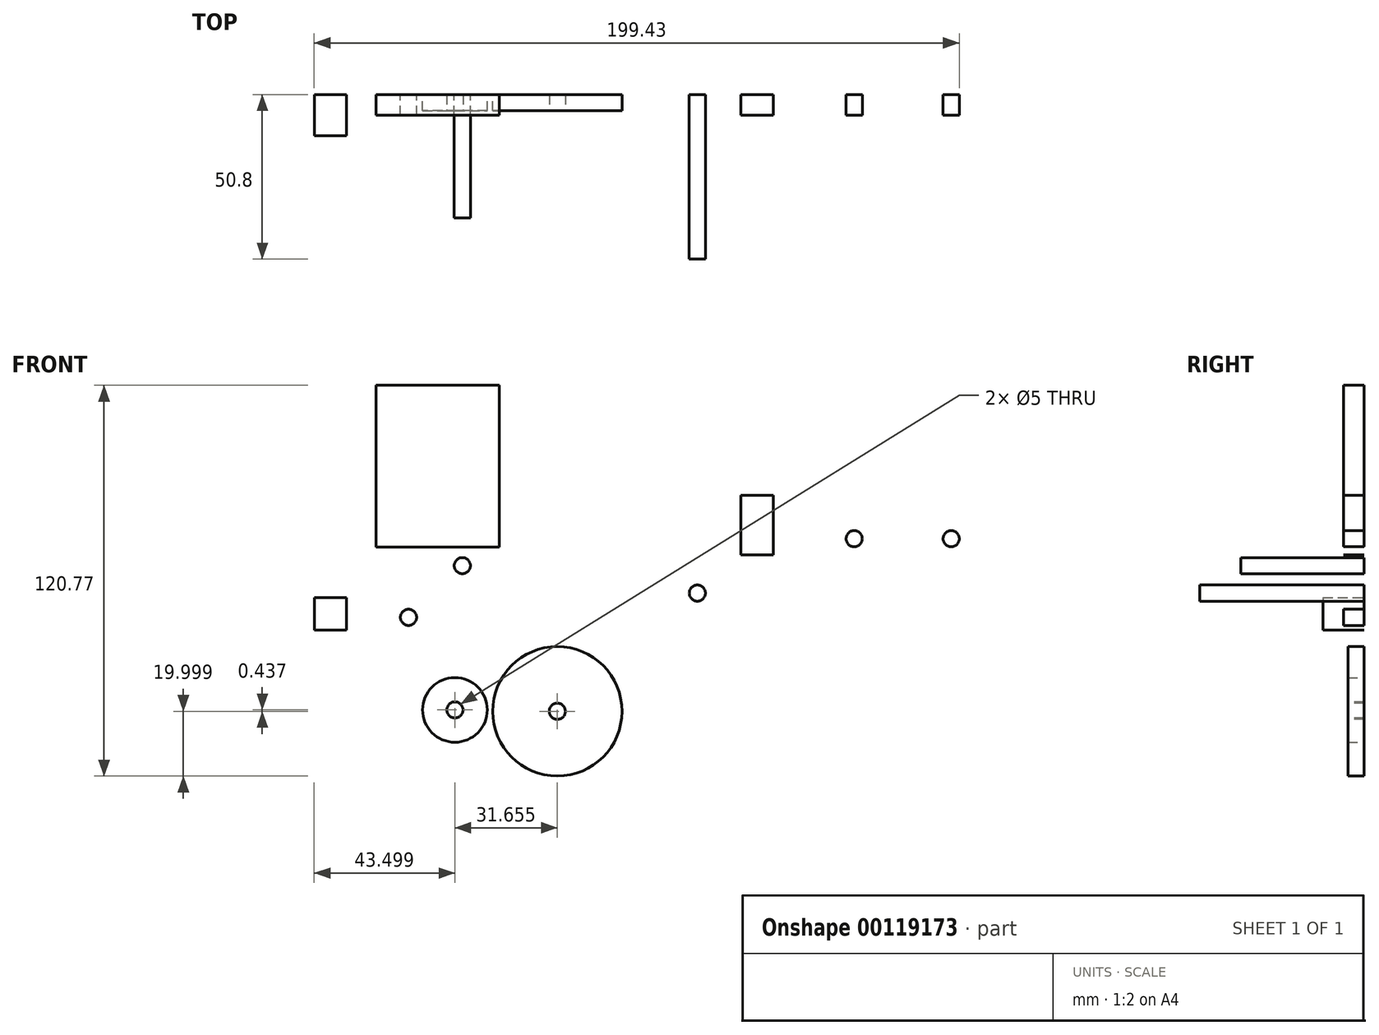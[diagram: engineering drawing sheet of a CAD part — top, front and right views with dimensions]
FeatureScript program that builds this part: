
annotation { "Feature Type Name" : "Feature", "Feature Type Description" : "" }
export const myFeature = defineFeature(function(context is Context, id is Id, definition is map)
    precondition{}
    {
        {
            var Q0;
            Q0=qCreatedBy(makeId("Front.planeOp"),FACE);
            var sketch = newSketch(context, id + "F0", { "sketchPlane" : qUnion([Q0])});
            skCircle(sketch, "E0", {"center": v(-47.6, -11.02) * mm, "radius": 10 * mm});
            skCircle(sketch, "E1", {"center": v(-15.94, -11.46) * mm, "radius": 20 * mm});
            skSolve(sketch);
        }
        {
            var Q0;
            Q0 = qSketchRegion(id + "F0", true);
            extrude(context, id + "F1", {"entities" : qUnion([Q0]), "depth" : 5 * mm});
        }
        {
            var Q0;
            Q0=makeQuery(id+"F1.opExtrude","CAP_FACE",FACE,{"disambiguationData":[OSD([sQuery(id+"F0.wireOp",EDGE,"E0")])],"isStart":false});
            var sketch = newSketch(context, id + "F2", { "sketchPlane" : qUnion([Q0])});
            skCircle(sketch, "E2", {"center": v(-47.6, -11.02) * mm, "radius": 2.5 * mm});
            skSolve(sketch);
        }
        {
            var Q0;
            Q0 = qSketchRegion(id + "F2", true);
            extrude(context, id + "F3", {"entities" : qUnion([Q0]), "operationType" : NewBodyOperationType.REMOVE, "endBound" : BoundingType.THROUGH_ALL, "oppositeDirection" : true, "depth" : 25.4 * mm});
        }
        {
            var Q0;
            Q0=makeQuery(id+"F1.opExtrude","CAP_FACE",FACE,{"disambiguationData":[OSD([sQuery(id+"F0.wireOp",EDGE,"E1")])],"isStart":false});
            var sketch = newSketch(context, id + "F4", { "sketchPlane" : qUnion([Q0])});
            skCircle(sketch, "E3", {"center": v(-15.94, -11.46) * mm, "radius": 2.5 * mm});
            skSolve(sketch);
        }
        {
            var Q0;
            Q0 = qSketchRegion(id + "F4", true);
            extrude(context, id + "F5", {"entities" : qUnion([Q0]), "operationType" : NewBodyOperationType.REMOVE, "endBound" : BoundingType.THROUGH_ALL, "oppositeDirection" : true, "depth" : 25.4 * mm});
        }
        {
            var Q0;
            Q0=qCreatedBy(makeId("Front.planeOp"),FACE);
            var sketch = newSketch(context, id + "F6", { "sketchPlane" : qUnion([Q0])});
            skCircle(sketch, "E4", {"center": v(-45.3, 33.56) * mm, "radius": 2.5 * mm});
            skSolve(sketch);
        }
        {
            var Q0;
            Q0 = qSketchRegion(id + "F6", true);
            extrude(context, id + "F7", {"entities" : qUnion([Q0]), "depth" : 38.1 * mm});
        }
        {
            var Q0;
            Q0=qCreatedBy(makeId("Front.planeOp"),FACE);
            var sketch = newSketch(context, id + "F8", { "sketchPlane" : qUnion([Q0])});
            skCircle(sketch, "E5", {"center": v(27.36, 25.08) * mm, "radius": 2.5 * mm});
            skSolve(sketch);
        }
        {
            var Q0;
            Q0 = qSketchRegion(id + "F8", true);
            extrude(context, id + "F9", {"entities" : qUnion([Q0]), "depth" : 50.8 * mm});
        }
        {
            var Q0;
            Q0=qCreatedBy(makeId("Front.planeOp"),FACE);
            var sketch = newSketch(context, id + "F10", { "sketchPlane" : qUnion([Q0])});
            skLineSegment(sketch, "E6.bottom", {"start": v(-71.97, 89.31) * mm, "end": v(-33.87, 89.31) * mm});
            skLineSegment(sketch, "E6.top", {"start": v(-71.97, 39.31) * mm, "end": v(-33.87, 39.31) * mm});
            skLineSegment(sketch, "E6.left", {"start": v(-71.97, 89.31) * mm, "end": v(-71.97, 39.31) * mm});
            skLineSegment(sketch, "E6.right", {"start": v(-33.87, 89.31) * mm, "end": v(-33.87, 39.31) * mm});
            skLineSegment(sketch, "E7.bottom", {"start": v(35.84, 66.88) * mm, "end": v(125.84, 66.88) * mm});
            skLineSegment(sketch, "E7.top", {"start": v(35.84, 16.88) * mm, "end": v(125.84, 16.88) * mm});
            skLineSegment(sketch, "E7.left", {"start": v(35.84, 66.88) * mm, "end": v(35.84, 16.88) * mm});
            skLineSegment(sketch, "E7.right", {"start": v(125.84, 66.88) * mm, "end": v(125.84, 16.88) * mm});
            skSolve(sketch);
        }
        {
            var Q0;
            Q0 = qSketchRegion(id + "F10", true);
            extrude(context, id + "F11", {"entities" : qUnion([Q0]), "operationType" : NewBodyOperationType.ADD, "depth" : 6.35 * mm});
        }
        {
            var Q0;
            Q0=makeQuery(id+"F11.opExtrude","CAP_FACE",FACE,{"disambiguationData":[OSD([sQuery(id+"F10.wireOp",EDGE,"E7.bottom"),sQuery(id+"F10.wireOp",EDGE,"E7.top"),sQuery(id+"F10.wireOp",EDGE,"E7.left"),sQuery(id+"F10.wireOp",EDGE,"E7.right")])],"isStart":false});
            var sketch = newSketch(context, id + "F12", { "sketchPlane" : qUnion([Q0])});
            skLineSegment(sketch, "E8", {"start": v(35.84, 41.88) * mm, "end": v(125.84, 41.88) * mm});
            skLineSegment(sketch, "E9.bottom", {"start": v(40.84, 41.88) * mm, "end": v(50.84, 41.88) * mm});
            skLineSegment(sketch, "E9.top", {"start": v(40.84, 36.88) * mm, "end": v(50.84, 36.88) * mm});
            skLineSegment(sketch, "E9.left", {"start": v(40.84, 41.88) * mm, "end": v(40.84, 36.88) * mm});
            skLineSegment(sketch, "E9.right", {"start": v(50.84, 41.88) * mm, "end": v(50.84, 36.88) * mm});
            skLineSegment(sketch, "E10.bottom", {"start": v(40.84, 41.88) * mm, "end": v(40.84, 41.88) * mm});
            skLineSegment(sketch, "E10.top", {"start": v(40.84, 55.33) * mm, "end": v(40.84, 55.33) * mm});
            skLineSegment(sketch, "E10.left", {"start": v(40.84, 41.88) * mm, "end": v(40.84, 55.33) * mm});
            skLineSegment(sketch, "E10.right", {"start": v(40.84, 41.88) * mm, "end": v(40.84, 55.33) * mm});
            skLineSegment(sketch, "E11.bottom", {"start": v(50.84, 41.88) * mm, "end": v(50.84, 41.88) * mm});
            skLineSegment(sketch, "E11.top", {"start": v(50.84, 46.88) * mm, "end": v(50.84, 46.88) * mm});
            skLineSegment(sketch, "E11.left", {"start": v(50.84, 41.88) * mm, "end": v(50.84, 46.88) * mm});
            skLineSegment(sketch, "E11.right", {"start": v(50.84, 41.88) * mm, "end": v(50.84, 46.88) * mm});
            skLineSegment(sketch, "E12.bottom", {"start": v(40.84, 55.33) * mm, "end": v(50.84, 55.33) * mm});
            skLineSegment(sketch, "E12.top", {"start": v(40.84, 46.88) * mm, "end": v(50.84, 46.88) * mm});
            skLineSegment(sketch, "E12.left", {"start": v(40.84, 46.88) * mm, "end": v(40.84, 55.33) * mm});
            skLineSegment(sketch, "E12.right", {"start": v(50.84, 46.88) * mm, "end": v(50.84, 55.33) * mm});
            skCircle(sketch, "E13", {"center": v(75.84, 41.88) * mm, "radius": 2.5 * mm});
            skCircle(sketch, "E14", {"center": v(105.84, 41.88) * mm, "radius": 2.5 * mm});
            skSolve(sketch);
        }
        {
            var Q0;
            {var subQ0=sQuery(id+"F12.wireOp",EDGE,"E13");var subQ1=sQuery(id+"F12.wireOp",EDGE,"E8");var subQ2=makeQuery(id+"F12.imprint","INTERSECT",VERTEX,{"disambiguationData":[OD(0.0)],"derivedFrom":[subQ1,subQ0]});Q0=makeQuery(id+"F12.imprint","IMPRINT",FACE,{"disambiguationData":[TD([[makeQuery(id+"F12.imprint","IMPRINT",EDGE,{"disambiguationData":[TD([[subQ2,-1.0]])],"derivedFrom":subQ1}),1.0]])]});}
            var Q1;
            {var subQ0=sQuery(id+"F12.wireOp",EDGE,"E13");var subQ1=sQuery(id+"F12.wireOp",EDGE,"E8");var subQ2=makeQuery(id+"F12.imprint","INTERSECT",VERTEX,{"disambiguationData":[OD(0.0)],"derivedFrom":[subQ1,subQ0]});Q1=makeQuery(id+"F12.imprint","IMPRINT",FACE,{"disambiguationData":[TD([[makeQuery(id+"F12.imprint","IMPRINT",EDGE,{"disambiguationData":[TD([[subQ2,-1.0]])],"derivedFrom":subQ1}),-1.0]])]});}
            var Q2;
            {var subQ0=sQuery(id+"F12.wireOp",EDGE,"E14");var subQ1=sQuery(id+"F12.wireOp",EDGE,"E8");var subQ2=makeQuery(id+"F12.imprint","INTERSECT",VERTEX,{"disambiguationData":[OD(0.0)],"derivedFrom":[subQ1,subQ0]});Q2=makeQuery(id+"F12.imprint","IMPRINT",FACE,{"disambiguationData":[TD([[makeQuery(id+"F12.imprint","IMPRINT",EDGE,{"disambiguationData":[TD([[subQ2,-1.0]])],"derivedFrom":subQ1}),1.0]])]});}
            var Q3;
            {var subQ0=sQuery(id+"F12.wireOp",EDGE,"E14");var subQ1=sQuery(id+"F12.wireOp",EDGE,"E8");var subQ2=makeQuery(id+"F12.imprint","INTERSECT",VERTEX,{"disambiguationData":[OD(0.0)],"derivedFrom":[subQ1,subQ0]});Q3=makeQuery(id+"F12.imprint","IMPRINT",FACE,{"disambiguationData":[TD([[makeQuery(id+"F12.imprint","IMPRINT",EDGE,{"disambiguationData":[TD([[subQ2,-1.0]])],"derivedFrom":subQ1}),-1.0]])]});}
            var Q4;
            Q4=makeQuery(id+"F12.imprint","IMPRINT",FACE,{"disambiguationData":[TD([[makeQuery(id+"F12.imprint","IMPRINT",EDGE,{"derivedFrom":sQuery(id+"F12.wireOp",EDGE,"E9.bottom")}),-1.0]])]});
            var Q5;
            Q5=makeQuery(id+"F12.imprint","IMPRINT",FACE,{"disambiguationData":[TD([[makeQuery(id+"F12.imprint","IMPRINT",EDGE,{"derivedFrom":sQuery(id+"F12.wireOp",EDGE,"E9.bottom")}),1.0]])]});
            extrude(context, id + "F13", {"entities" : qUnion([Q0, Q1, Q2, Q3, Q4, Q5]), "operationType" : NewBodyOperationType.REMOVE, "endBound" : BoundingType.THROUGH_ALL, "oppositeDirection" : true, "depth" : 25.4 * mm});
        }
        {
            var Q0;
            Q0=qCreatedBy(makeId("Front.planeOp"),FACE);
            var sketch = newSketch(context, id + "F14", { "sketchPlane" : qUnion([Q0])});
            skLineSegment(sketch, "E15.bottom", {"start": v(-91.09, 23.65) * mm, "end": v(-81.09, 23.65) * mm});
            skLineSegment(sketch, "E15.top", {"start": v(-91.09, 13.65) * mm, "end": v(-81.09, 13.65) * mm});
            skLineSegment(sketch, "E15.left", {"start": v(-91.09, 23.65) * mm, "end": v(-91.09, 13.65) * mm});
            skLineSegment(sketch, "E15.right", {"start": v(-81.09, 23.65) * mm, "end": v(-81.09, 13.65) * mm});
            skSolve(sketch);
        }
        {
            var Q0;
            Q0 = qSketchRegion(id + "F14", true);
            extrude(context, id + "F15", {"entities" : qUnion([Q0]), "depth" : 12.7 * mm});
        }
        {
            var Q0;
            Q0=qCreatedBy(makeId("Front.planeOp"),FACE);
            var sketch = newSketch(context, id + "F16", { "sketchPlane" : qUnion([Q0])});
            skCircle(sketch, "E16", {"center": v(-61.93, 17.58) * mm, "radius": 2.5 * mm});
            skSolve(sketch);
        }
        {
            var Q0;
            Q0 = qSketchRegion(id + "F16", true);
            extrude(context, id + "F17", {"entities" : qUnion([Q0]), "depth" : 6.35 * mm});
        }
    });
